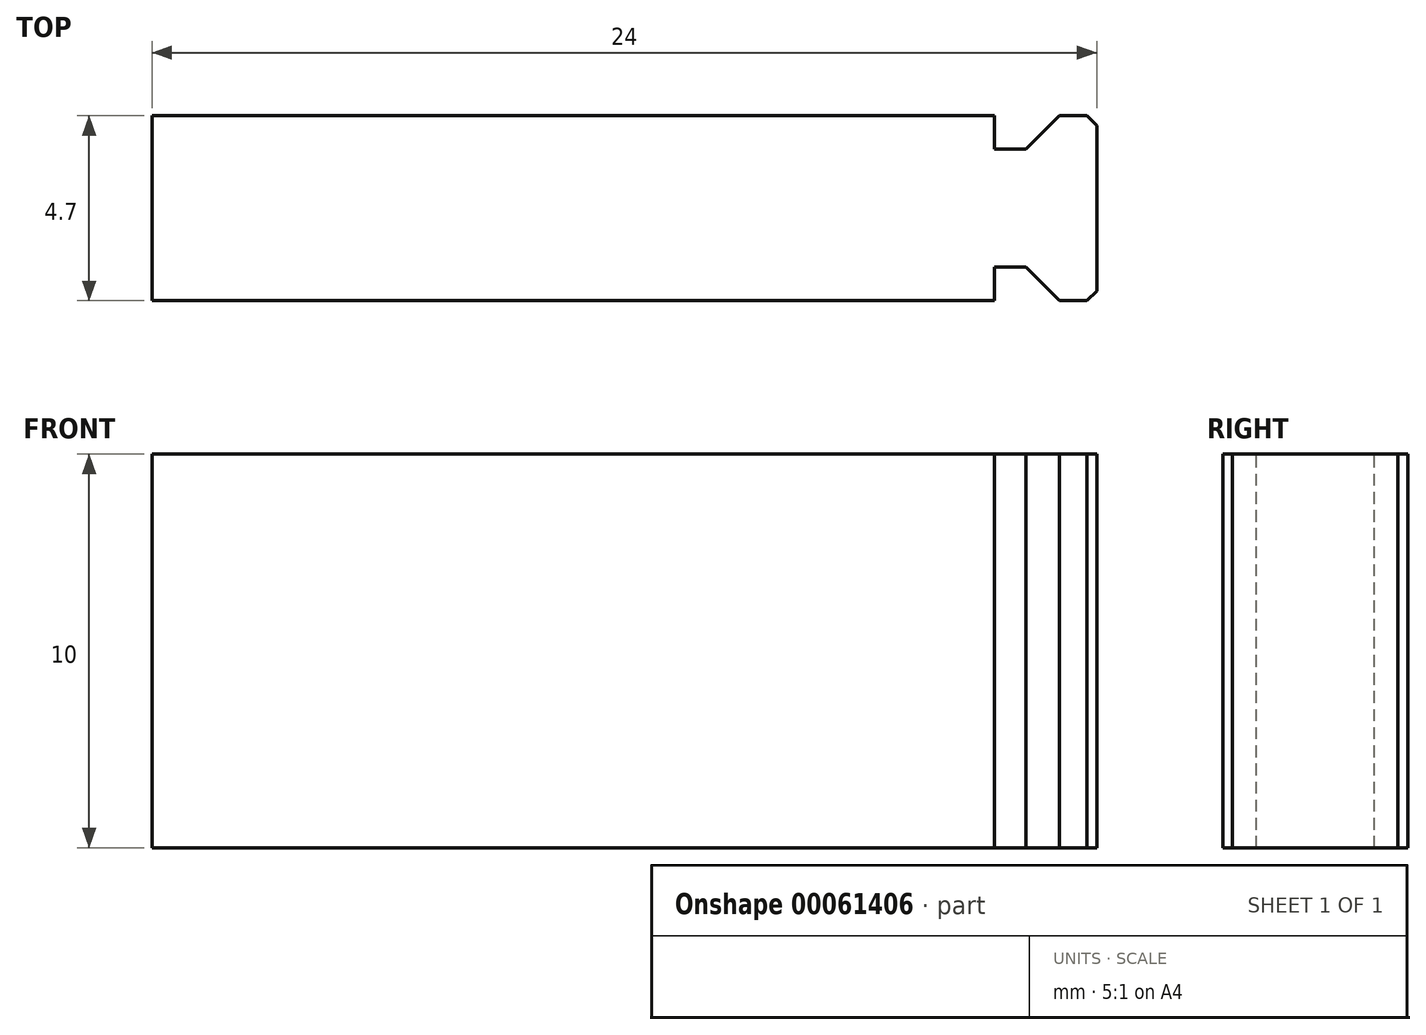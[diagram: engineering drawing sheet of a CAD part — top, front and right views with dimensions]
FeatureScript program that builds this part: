
annotation { "Feature Type Name" : "Feature", "Feature Type Description" : "" }
export const myFeature = defineFeature(function(context is Context, id is Id, definition is map)
    precondition{}
    {
        {
            var Q0;
            Q0=qCreatedBy(makeId("Top.planeOp"),FACE);
            var sketch = newSketch(context, id + "F0", { "sketchPlane" : qUnion([Q0])});
            skLineSegment(sketch, "E0", {"start": v(21.4, 1.5) * mm, "end": v(22.2, 1.5) * mm});
            skLineSegment(sketch, "E1", {"start": v(22.2, 1.5) * mm, "end": v(23.05, 2.35) * mm});
            skLineSegment(sketch, "E2", {"start": v(23.05, 2.35) * mm, "end": v(23.75, 2.35) * mm});
            skLineSegment(sketch, "E3", {"start": v(23.75, 2.35) * mm, "end": v(24, 2.1) * mm});
            skLineSegment(sketch, "E4", {"start": v(24, 2.1) * mm, "end": v(24, 0) * mm});
            skLineSegment(sketch, "E5", {"start": v(0, 0) * mm, "end": v(24, 0) * mm, "construction": true});
            skLineSegment(sketch, "E6", {"start": v(21.4, 1.5) * mm, "end": v(21.4, 2.35) * mm});
            skLineSegment(sketch, "E7", {"start": v(21.4, 2.35) * mm, "end": v(0, 2.35) * mm});
            skLineSegment(sketch, "E8", {"start": v(0, 2.35) * mm, "end": v(0, 0) * mm});
            skLineSegment(sketch, "E9", {"start": v(21.8, 1.5) * mm, "end": v(21.8, 0.38) * mm, "construction": true});
            skLineSegment(sketch, "E10.MirrorCS", {"start": v(23.05, -2.35) * mm, "end": v(23.75, -2.35) * mm});
            skLineSegment(sketch, "E11.MirrorCS", {"start": v(23.75, -2.35) * mm, "end": v(24, -2.1) * mm});
            skLineSegment(sketch, "E12.MirrorCS", {"start": v(21.4, -1.5) * mm, "end": v(22.2, -1.5) * mm});
            skLineSegment(sketch, "E13.MirrorCS", {"start": v(21.4, -2.35) * mm, "end": v(0, -2.35) * mm});
            skLineSegment(sketch, "E14.MirrorCS", {"start": v(0, -2.35) * mm, "end": v(0, 0) * mm});
            skLineSegment(sketch, "E15.MirrorCS", {"start": v(24, -2.1) * mm, "end": v(24, 0) * mm});
            skLineSegment(sketch, "E16.MirrorCS", {"start": v(21.4, -1.5) * mm, "end": v(21.4, -2.35) * mm});
            skLineSegment(sketch, "E17.MirrorCS", {"start": v(21.8, -1.5) * mm, "end": v(21.8, -0.38) * mm, "construction": true});
            skLineSegment(sketch, "E18.MirrorCS", {"start": v(22.2, -1.5) * mm, "end": v(23.05, -2.35) * mm});
            skSolve(sketch);
        }
        {
            var Q0;
            Q0=makeQuery(id+"F0.imprint","IMPRINT",FACE,{"disambiguationData":[TD([[makeQuery(id+"F0.imprint","IMPRINT",EDGE,{"derivedFrom":sQuery(id+"F0.wireOp",EDGE,"E0")}),-1.0]])]});
            extrude(context, id + "F1", {"entities" : qUnion([Q0]), "oppositeDirection" : true, "depth" : 10 * mm});
        }
    });
